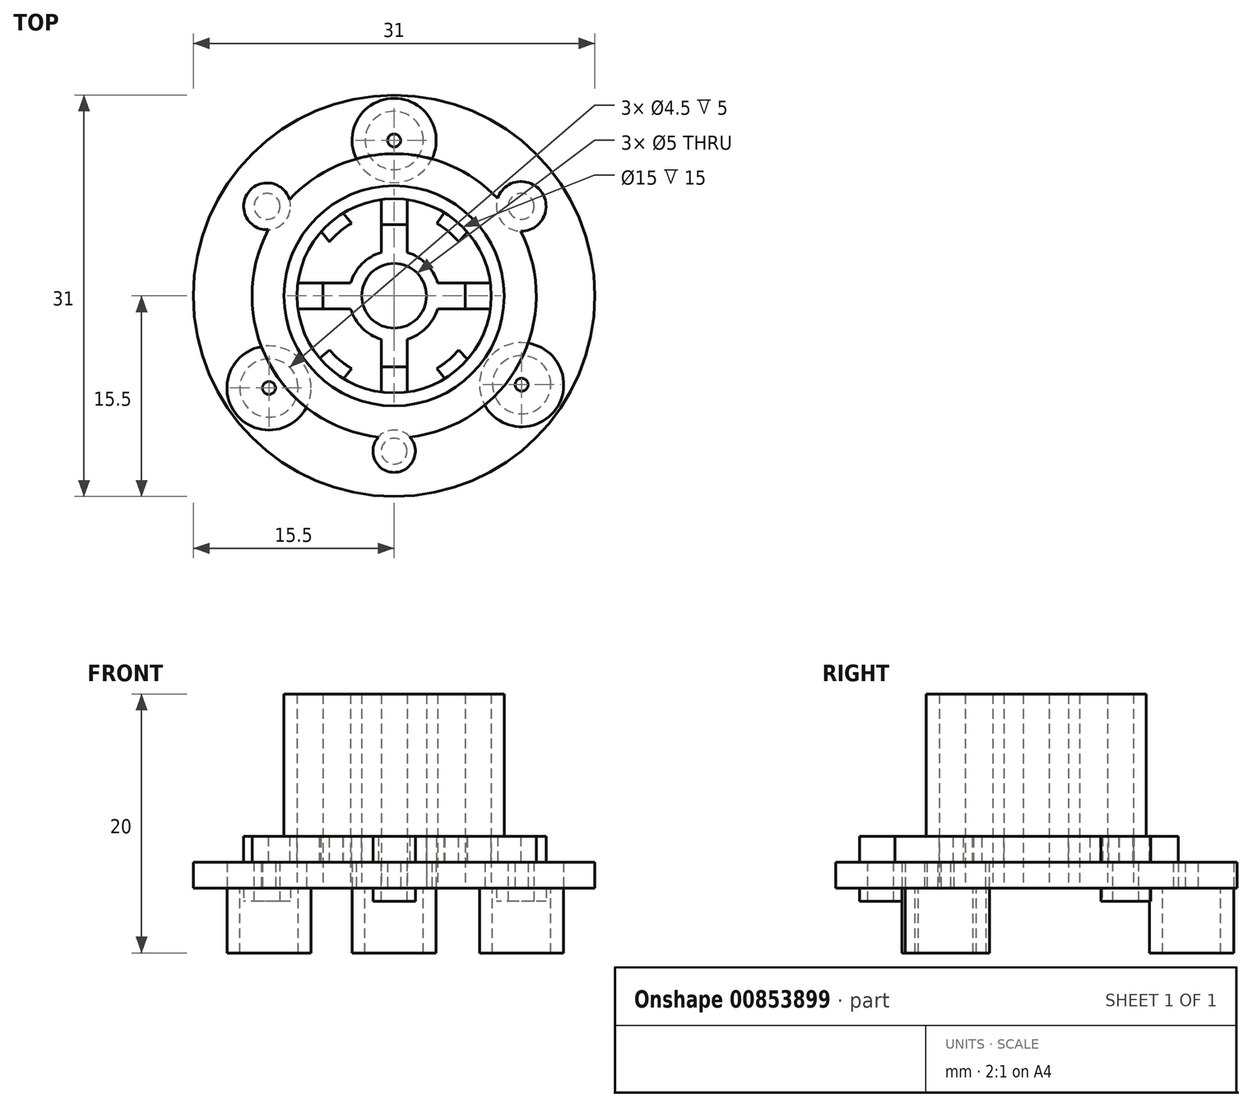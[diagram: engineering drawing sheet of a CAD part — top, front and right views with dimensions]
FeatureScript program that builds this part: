
annotation { "Feature Type Name" : "Feature", "Feature Type Description" : "" }
export const myFeature = defineFeature(function(context is Context, id is Id, definition is map)
    precondition{}
    {
        {
            var Q0;
            Q0=qCreatedBy(makeId("Top.planeOp"),FACE);
            var sketch = newSketch(context, id + "F0", { "sketchPlane" : qUnion([Q0])});
            skCircle(sketch, "E0", {"center": v(0, 0) * mm, "radius": 15.5 * mm});
            skCircle(sketch, "E1", {"center": v(0, 0) * mm, "radius": 8.5 * mm});
            skCircle(sketch, "E2.0", {"center": v(0, 0) * mm, "radius": 7.5 * mm});
            skLineSegment(sketch, "E3", {"start": v(-15.5, 0) * mm, "end": v(15.5, 0) * mm});
            skCircle(sketch, "E4", {"center": v(0, 0) * mm, "radius": 12 * mm});
            skCircle(sketch, "E5", {"center": v(0, 12) * mm, "radius": 3.25 * mm});
            skCircle(sketch, "E6", {"center": v(-9.66, -7.12) * mm, "radius": 3.25 * mm});
            skCircle(sketch, "E7", {"center": v(9.84, -6.87) * mm, "radius": 3.25 * mm});
            skCircle(sketch, "E8.0", {"center": v(-9.66, -7.12) * mm, "radius": 2.25 * mm});
            skCircle(sketch, "E9.0", {"center": v(9.84, -6.87) * mm, "radius": 2.25 * mm});
            skCircle(sketch, "E10.0", {"center": v(0, 12) * mm, "radius": 2.25 * mm});
            skCircle(sketch, "E11", {"center": v(0, -12) * mm, "radius": 1 * mm});
            skCircle(sketch, "E12", {"center": v(-9.81, 6.91) * mm, "radius": 1 * mm});
            skCircle(sketch, "E13", {"center": v(9.81, 6.91) * mm, "radius": 1 * mm});
            skCircle(sketch, "E14", {"center": v(0, 0) * mm, "radius": 10.97 * mm});
            skCircle(sketch, "E15", {"center": v(0, -12) * mm, "radius": 1.64 * mm});
            skCircle(sketch, "E16", {"center": v(9.81, 6.91) * mm, "radius": 1.92 * mm});
            skCircle(sketch, "E17", {"center": v(-9.81, 6.91) * mm, "radius": 1.8 * mm});
            skCircle(sketch, "E18", {"center": v(-9.66, -7.12) * mm, "radius": 0.5 * mm});
            skCircle(sketch, "E19", {"center": v(9.84, -6.87) * mm, "radius": 0.5 * mm});
            skCircle(sketch, "E20", {"center": v(0, 12) * mm, "radius": 0.5 * mm});
            skCircle(sketch, "E21", {"center": v(0, 0) * mm, "radius": 2.5 * mm});
            skLineSegment(sketch, "E22.bottom", {"start": v(1, -5.5) * mm, "end": v(-1, -5.5) * mm});
            skLineSegment(sketch, "E22.top", {"start": v(1, 5.5) * mm, "end": v(-1, 5.5) * mm});
            skLineSegment(sketch, "E22.left", {"start": v(1, -5.5) * mm, "end": v(1, 5.5) * mm});
            skLineSegment(sketch, "E22.right", {"start": v(-1, -5.5) * mm, "end": v(-1, 5.5) * mm});
            skLineSegment(sketch, "E23.bottom", {"start": v(5.5, -1) * mm, "end": v(-5.5, -1) * mm});
            skLineSegment(sketch, "E23.top", {"start": v(5.5, 1) * mm, "end": v(-5.5, 1) * mm});
            skLineSegment(sketch, "E23.left", {"start": v(5.5, -1) * mm, "end": v(5.5, 1) * mm});
            skLineSegment(sketch, "E23.right", {"start": v(-5.5, -1) * mm, "end": v(-5.5, 1) * mm});
            skCircle(sketch, "E24.0", {"center": v(0, 0) * mm, "radius": 3.5 * mm});
            skLineSegment(sketch, "E25", {"start": v(-5.5, -1) * mm, "end": v(-7.43, -1) * mm});
            skLineSegment(sketch, "E26", {"start": v(-5.5, 1) * mm, "end": v(-7.43, 1) * mm});
            skLineSegment(sketch, "E27", {"start": v(5.5, -1) * mm, "end": v(7.43, -1) * mm});
            skLineSegment(sketch, "E28", {"start": v(5.5, 1) * mm, "end": v(7.43, 1) * mm});
            skLineSegment(sketch, "E29", {"start": v(-1, -5.5) * mm, "end": v(-1, -7.43) * mm});
            skLineSegment(sketch, "E30", {"start": v(1, -5.5) * mm, "end": v(1, -7.43) * mm});
            skLineSegment(sketch, "E31", {"start": v(-1, 5.5) * mm, "end": v(-1, 7.43) * mm});
            skLineSegment(sketch, "E32", {"start": v(1, 5.5) * mm, "end": v(1, 7.43) * mm});
            skSolve(sketch);
        }
        {
            var Q0;
            Q0=makeQuery(id+"F0.imprint","IMPRINT",FACE,{"disambiguationData":[TD([[makeQuery(id+"F0.imprint","IMPRINT",EDGE,{"derivedFrom":sQuery(id+"F0.wireOp",EDGE,"E0")}),1.0]])]});
            var Q1;
            {var subQ0=sQuery(id+"F0.wireOp",EDGE,"S9bKF7eP-WOtO-HVjA-zyf9-2dM2ckVghxGc");var subQ4=sQuery(id+"F0.wireOp",EDGE,"a8cJaAZh-5I12-enwt-A6UE-ITXqOD4lF9Ac");var subQ5=makeQuery(id+"F0.imprint","INTERSECT",VERTEX,{"disambiguationData":[OD(0.0)],"derivedFrom":[subQ0,subQ4]});Q1=makeQuery(id+"F0.imprint","IMPRINT",FACE,{"disambiguationData":[TD([[makeQuery(id+"F0.imprint","IMPRINT",EDGE,{"disambiguationData":[TD([[subQ5,1.0]])],"derivedFrom":subQ4}),-1.0]])]});}
            var Q2;
            {var subQ1=sQuery(id+"F0.wireOp",EDGE,"E3");var subQ4=sQuery(id+"F0.wireOp",EDGE,"E1");var subQ11=makeQuery(id+"F0.imprint","INTERSECT",VERTEX,{"disambiguationData":[OD(0.0)],"derivedFrom":[subQ4,subQ1]});Q2=makeQuery(id+"F0.imprint","IMPRINT",FACE,{"disambiguationData":[TD([[makeQuery(id+"F0.imprint","IMPRINT",EDGE,{"disambiguationData":[TD([[subQ11,-1.0]])],"derivedFrom":subQ4}),-1.0]])]});}
            var Q3;
            {var subQ5=sQuery(id+"F0.wireOp",EDGE,"ll5ePz1X-QG4W-kVrY-982M-5qMvGsVVYmu8");Q3=makeQuery(id+"F0.imprint","IMPRINT",FACE,{"disambiguationData":[TD([[makeQuery(id+"F0.imprint","IMPRINT",EDGE,{"derivedFrom":subQ5}),-1.0]])]});}
            var Q4;
            {var subQ0=sQuery(id+"F0.wireOp",EDGE,"Ehf1EnBC-OwnA-8WcZ-1eJj-KpamyHMtwVbQ");var subQ4=sQuery(id+"F0.wireOp",EDGE,"xySDpFPR-NNtx-CsFH-j8Qs-mnjDACDE4txv");var subQ5=makeQuery(id+"F0.imprint","INTERSECT",VERTEX,{"disambiguationData":[OD(0.0)],"derivedFrom":[subQ0,subQ4]});Q4=makeQuery(id+"F0.imprint","IMPRINT",FACE,{"disambiguationData":[TD([[makeQuery(id+"F0.imprint","IMPRINT",EDGE,{"disambiguationData":[TD([[subQ5,1.0]])],"derivedFrom":subQ4}),-1.0]])]});}
            var Q5;
            {var subQ1=sQuery(id+"F0.wireOp",EDGE,"E3");var subQ5=sQuery(id+"F0.wireOp",EDGE,"E1");var subQ6=makeQuery(id+"F0.imprint","INTERSECT",VERTEX,{"disambiguationData":[OD(0.0)],"derivedFrom":[subQ5,subQ1]});Q5=makeQuery(id+"F0.imprint","IMPRINT",FACE,{"disambiguationData":[TD([[makeQuery(id+"F0.imprint","IMPRINT",EDGE,{"disambiguationData":[TD([[subQ6,1.0]])],"derivedFrom":subQ5}),-1.0]])]});}
            var Q6;
            {var subQ0=sQuery(id+"F0.wireOp",EDGE,"E3");var subQ1=sQuery(id+"F0.wireOp",EDGE,"E0");var subQ5=makeQuery(id+"F0.imprint","INTERSECT",VERTEX,{"disambiguationData":[OD(0.0)],"derivedFrom":[subQ1,subQ0]});Q6=makeQuery(id+"F0.imprint","IMPRINT",FACE,{"disambiguationData":[TD([[makeQuery(id+"F0.imprint","IMPRINT",EDGE,{"disambiguationData":[TD([[subQ5,-1.0]])],"derivedFrom":subQ1}),1.0]])]});}
            var Q7;
            {var subQ0=sQuery(id+"F0.wireOp",EDGE,"E6");var subQ1=sQuery(id+"F0.wireOp",EDGE,"E4");var subQ2=makeQuery(id+"F0.imprint","INTERSECT",VERTEX,{"disambiguationData":[OD(1.0)],"derivedFrom":[subQ1,subQ0]});Q7=makeQuery(id+"F0.imprint","IMPRINT",FACE,{"disambiguationData":[TD([[makeQuery(id+"F0.imprint","IMPRINT",EDGE,{"disambiguationData":[TD([[subQ2,-1.0]])],"derivedFrom":subQ1}),1.0]])]});}
            var Q8;
            {var subQ0=sQuery(id+"F0.wireOp",EDGE,"E4");var subQ1=sQuery(id+"F0.wireOp",EDGE,"E3");var subQ2=makeQuery(id+"F0.imprint","INTERSECT",VERTEX,{"disambiguationData":[OD(0.0)],"derivedFrom":[subQ1,subQ0]});Q8=makeQuery(id+"F0.imprint","IMPRINT",FACE,{"disambiguationData":[TD([[makeQuery(id+"F0.imprint","IMPRINT",EDGE,{"disambiguationData":[TD([[subQ2,-1.0]])],"derivedFrom":subQ1}),-1.0]])]});}
            var Q9;
            {var subQ0=sQuery(id+"F0.wireOp",EDGE,"E4");var subQ1=sQuery(id+"F0.wireOp",EDGE,"E3");var subQ2=makeQuery(id+"F0.imprint","INTERSECT",VERTEX,{"disambiguationData":[OD(0.0)],"derivedFrom":[subQ1,subQ0]});Q9=makeQuery(id+"F0.imprint","IMPRINT",FACE,{"disambiguationData":[TD([[makeQuery(id+"F0.imprint","IMPRINT",EDGE,{"disambiguationData":[TD([[subQ2,-1.0]])],"derivedFrom":subQ1}),1.0]])]});}
            var Q10;
            {var subQ0=sQuery(id+"F0.wireOp",EDGE,"E5");var subQ1=sQuery(id+"F0.wireOp",EDGE,"E4");var subQ2=makeQuery(id+"F0.imprint","INTERSECT",VERTEX,{"disambiguationData":[OD(1.0)],"derivedFrom":[subQ1,subQ0]});Q10=makeQuery(id+"F0.imprint","IMPRINT",FACE,{"disambiguationData":[TD([[makeQuery(id+"F0.imprint","IMPRINT",EDGE,{"disambiguationData":[TD([[subQ2,-1.0]])],"derivedFrom":subQ1}),1.0]])]});}
            var Q11;
            {var subQ0=sQuery(id+"F0.wireOp",EDGE,"E16");var subQ1=sQuery(id+"F0.wireOp",EDGE,"E4");var subQ2=makeQuery(id+"F0.imprint","INTERSECT",VERTEX,{"disambiguationData":[OD(1.0)],"derivedFrom":[subQ1,subQ0]});Q11=makeQuery(id+"F0.imprint","IMPRINT",FACE,{"disambiguationData":[TD([[makeQuery(id+"F0.imprint","IMPRINT",EDGE,{"disambiguationData":[TD([[subQ2,-1.0]])],"derivedFrom":subQ1}),1.0]])]});}
            var Q12;
            {var subQ0=sQuery(id+"F0.wireOp",EDGE,"E14");var subQ1=sQuery(id+"F0.wireOp",EDGE,"E3");var subQ2=makeQuery(id+"F0.imprint","INTERSECT",VERTEX,{"disambiguationData":[OD(1.0)],"derivedFrom":[subQ1,subQ0]});Q12=makeQuery(id+"F0.imprint","IMPRINT",FACE,{"disambiguationData":[TD([[makeQuery(id+"F0.imprint","IMPRINT",EDGE,{"disambiguationData":[TD([[subQ2,-1.0]])],"derivedFrom":subQ1}),1.0]])]});}
            var Q13;
            {var subQ0=sQuery(id+"F0.wireOp",EDGE,"E14");var subQ1=sQuery(id+"F0.wireOp",EDGE,"E3");var subQ2=makeQuery(id+"F0.imprint","INTERSECT",VERTEX,{"disambiguationData":[OD(1.0)],"derivedFrom":[subQ1,subQ0]});Q13=makeQuery(id+"F0.imprint","IMPRINT",FACE,{"disambiguationData":[TD([[makeQuery(id+"F0.imprint","IMPRINT",EDGE,{"disambiguationData":[TD([[subQ2,-1.0]])],"derivedFrom":subQ1}),-1.0]])]});}
            var Q14;
            {var subQ0=sQuery(id+"F0.wireOp",EDGE,"E15");var subQ1=sQuery(id+"F0.wireOp",EDGE,"E4");var subQ2=makeQuery(id+"F0.imprint","INTERSECT",VERTEX,{"disambiguationData":[OD(1.0)],"derivedFrom":[subQ1,subQ0]});Q14=makeQuery(id+"F0.imprint","IMPRINT",FACE,{"disambiguationData":[TD([[makeQuery(id+"F0.imprint","IMPRINT",EDGE,{"disambiguationData":[TD([[subQ2,-1.0]])],"derivedFrom":subQ1}),1.0]])]});}
            extrude(context, id + "F1", {"entities" : qUnion([Q0, Q1, Q2, Q3, Q4, Q5, Q6, Q7, Q8, Q9, Q10, Q11, Q12, Q13, Q14]), "depth" : 2 * mm, "offsetDistance" : 25 * mm});
        }
        {
            var Q0;
            Q0=makeQuery(id+"F0.imprint","IMPRINT",FACE,{"disambiguationData":[TD([[makeQuery(id+"F0.imprint","IMPRINT",EDGE,{"derivedFrom":sQuery(id+"F0.wireOp",EDGE,"E1")}),1.0]])]});
            extrude(context, id + "F2", {"entities" : qUnion([Q0]), "operationType" : NewBodyOperationType.ADD, "depth" : 15 * mm, "offsetDistance" : 25 * mm});
        }
        {
            var Q0;
            {var subQ0=sQuery(id+"F0.wireOp",EDGE,"E5");var subQ1=sQuery(id+"F0.wireOp",EDGE,"E4");var subQ2=makeQuery(id+"F0.imprint","INTERSECT",VERTEX,{"disambiguationData":[OD(0.0)],"derivedFrom":[subQ1,subQ0]});Q0=makeQuery(id+"F0.imprint","IMPRINT",FACE,{"disambiguationData":[TD([[makeQuery(id+"F0.imprint","IMPRINT",EDGE,{"disambiguationData":[TD([[subQ2,-1.0]])],"derivedFrom":subQ1}),-1.0]])]});}
            var Q1;
            {var subQ0=sQuery(id+"F0.wireOp",EDGE,"E5");var subQ1=sQuery(id+"F0.wireOp",EDGE,"E4");var subQ2=makeQuery(id+"F0.imprint","INTERSECT",VERTEX,{"disambiguationData":[OD(0.0)],"derivedFrom":[subQ1,subQ0]});Q1=makeQuery(id+"F0.imprint","IMPRINT",FACE,{"disambiguationData":[TD([[makeQuery(id+"F0.imprint","IMPRINT",EDGE,{"disambiguationData":[TD([[subQ2,-1.0]])],"derivedFrom":subQ1}),1.0]])]});}
            var Q2;
            {var subQ0=sQuery(id+"F0.wireOp",EDGE,"E7");var subQ1=sQuery(id+"F0.wireOp",EDGE,"E4");var subQ2=makeQuery(id+"F0.imprint","INTERSECT",VERTEX,{"disambiguationData":[OD(0.0)],"derivedFrom":[subQ1,subQ0]});Q2=makeQuery(id+"F0.imprint","IMPRINT",FACE,{"disambiguationData":[TD([[makeQuery(id+"F0.imprint","IMPRINT",EDGE,{"disambiguationData":[TD([[subQ2,-1.0]])],"derivedFrom":subQ1}),1.0]])]});}
            var Q3;
            {var subQ0=sQuery(id+"F0.wireOp",EDGE,"E7");var subQ1=sQuery(id+"F0.wireOp",EDGE,"E4");var subQ2=makeQuery(id+"F0.imprint","INTERSECT",VERTEX,{"disambiguationData":[OD(0.0)],"derivedFrom":[subQ1,subQ0]});Q3=makeQuery(id+"F0.imprint","IMPRINT",FACE,{"disambiguationData":[TD([[makeQuery(id+"F0.imprint","IMPRINT",EDGE,{"disambiguationData":[TD([[subQ2,-1.0]])],"derivedFrom":subQ1}),-1.0]])]});}
            var Q4;
            {var subQ0=sQuery(id+"F0.wireOp",EDGE,"E6");var subQ1=sQuery(id+"F0.wireOp",EDGE,"E4");var subQ2=makeQuery(id+"F0.imprint","INTERSECT",VERTEX,{"disambiguationData":[OD(0.0)],"derivedFrom":[subQ1,subQ0]});Q4=makeQuery(id+"F0.imprint","IMPRINT",FACE,{"disambiguationData":[TD([[makeQuery(id+"F0.imprint","IMPRINT",EDGE,{"disambiguationData":[TD([[subQ2,-1.0]])],"derivedFrom":subQ1}),-1.0]])]});}
            var Q5;
            {var subQ0=sQuery(id+"F0.wireOp",EDGE,"E6");var subQ1=sQuery(id+"F0.wireOp",EDGE,"E4");var subQ2=makeQuery(id+"F0.imprint","INTERSECT",VERTEX,{"disambiguationData":[OD(0.0)],"derivedFrom":[subQ1,subQ0]});Q5=makeQuery(id+"F0.imprint","IMPRINT",FACE,{"disambiguationData":[TD([[makeQuery(id+"F0.imprint","IMPRINT",EDGE,{"disambiguationData":[TD([[subQ2,-1.0]])],"derivedFrom":subQ1}),1.0]])]});}
            var Q6;
            {var subQ0=sQuery(id+"F0.wireOp",EDGE,"E14");var subQ1=sQuery(id+"F0.wireOp",EDGE,"E6");var subQ2=makeQuery(id+"F0.imprint","INTERSECT",VERTEX,{"disambiguationData":[OD(0.0)],"derivedFrom":[subQ1,subQ0]});Q6=makeQuery(id+"F0.imprint","IMPRINT",FACE,{"disambiguationData":[TD([[makeQuery(id+"F0.imprint","IMPRINT",EDGE,{"disambiguationData":[TD([[subQ2,1.0]])],"derivedFrom":subQ1}),1.0]])]});}
            var Q7;
            {var subQ0=sQuery(id+"F0.wireOp",EDGE,"E8.0");var subQ1=sQuery(id+"F0.wireOp",EDGE,"E4");var subQ2=makeQuery(id+"F0.imprint","INTERSECT",VERTEX,{"disambiguationData":[OD(1.0)],"derivedFrom":[subQ1,subQ0]});Q7=makeQuery(id+"F0.imprint","IMPRINT",FACE,{"disambiguationData":[TD([[makeQuery(id+"F0.imprint","IMPRINT",EDGE,{"disambiguationData":[TD([[subQ2,-1.0]])],"derivedFrom":subQ1}),1.0]])]});}
            var Q8;
            {var subQ0=sQuery(id+"F0.wireOp",EDGE,"E14");var subQ1=sQuery(id+"F0.wireOp",EDGE,"E7");var subQ2=makeQuery(id+"F0.imprint","INTERSECT",VERTEX,{"disambiguationData":[OD(0.0)],"derivedFrom":[subQ1,subQ0]});Q8=makeQuery(id+"F0.imprint","IMPRINT",FACE,{"disambiguationData":[TD([[makeQuery(id+"F0.imprint","IMPRINT",EDGE,{"disambiguationData":[TD([[subQ2,-1.0]])],"derivedFrom":subQ1}),1.0]])]});}
            var Q9;
            {var subQ0=sQuery(id+"F0.wireOp",EDGE,"E9.0");var subQ1=sQuery(id+"F0.wireOp",EDGE,"E4");var subQ2=makeQuery(id+"F0.imprint","INTERSECT",VERTEX,{"disambiguationData":[OD(1.0)],"derivedFrom":[subQ1,subQ0]});Q9=makeQuery(id+"F0.imprint","IMPRINT",FACE,{"disambiguationData":[TD([[makeQuery(id+"F0.imprint","IMPRINT",EDGE,{"disambiguationData":[TD([[subQ2,-1.0]])],"derivedFrom":subQ1}),1.0]])]});}
            var Q10;
            {var subQ0=sQuery(id+"F0.wireOp",EDGE,"E14");var subQ1=sQuery(id+"F0.wireOp",EDGE,"E5");var subQ2=makeQuery(id+"F0.imprint","INTERSECT",VERTEX,{"disambiguationData":[OD(0.0)],"derivedFrom":[subQ1,subQ0]});Q10=makeQuery(id+"F0.imprint","IMPRINT",FACE,{"disambiguationData":[TD([[makeQuery(id+"F0.imprint","IMPRINT",EDGE,{"disambiguationData":[TD([[subQ2,-1.0]])],"derivedFrom":subQ1}),1.0]])]});}
            var Q11;
            {var subQ0=sQuery(id+"F0.wireOp",EDGE,"E10.0");var subQ1=sQuery(id+"F0.wireOp",EDGE,"E4");var subQ2=makeQuery(id+"F0.imprint","INTERSECT",VERTEX,{"disambiguationData":[OD(1.0)],"derivedFrom":[subQ1,subQ0]});Q11=makeQuery(id+"F0.imprint","IMPRINT",FACE,{"disambiguationData":[TD([[makeQuery(id+"F0.imprint","IMPRINT",EDGE,{"disambiguationData":[TD([[subQ2,-1.0]])],"derivedFrom":subQ1}),1.0]])]});}
            extrude(context, id + "F3", {"entities" : qUnion([Q0, Q1, Q2, Q3, Q4, Q5, Q6, Q7, Q8, Q9, Q10, Q11]), "depth" : -5 * mm, "offsetDistance" : 25 * mm});
        }
        {
            var Q0;
            {var subQ0=sQuery(id+"F0.wireOp",EDGE,"E3");var subQ1=sQuery(id+"F0.wireOp",EDGE,"E1");var subQ2=makeQuery(id+"F0.imprint","INTERSECT",VERTEX,{"disambiguationData":[OD(0.0)],"derivedFrom":[subQ1,subQ0]});Q0=makeQuery(id+"F0.imprint","IMPRINT",FACE,{"disambiguationData":[TD([[makeQuery(id+"F0.imprint","IMPRINT",EDGE,{"disambiguationData":[TD([[subQ2,1.0]])],"derivedFrom":subQ1}),-1.0]])]});}
            var Q1;
            {var subQ0=sQuery(id+"F0.wireOp",EDGE,"E3");var subQ1=sQuery(id+"F0.wireOp",EDGE,"E1");var subQ11=makeQuery(id+"F0.imprint","INTERSECT",VERTEX,{"disambiguationData":[OD(0.0)],"derivedFrom":[subQ1,subQ0]});Q1=makeQuery(id+"F0.imprint","IMPRINT",FACE,{"disambiguationData":[TD([[makeQuery(id+"F0.imprint","IMPRINT",EDGE,{"disambiguationData":[TD([[subQ11,-1.0]])],"derivedFrom":subQ1}),-1.0]])]});}
            var Q2;
            {var subQ0=sQuery(id+"F0.wireOp",EDGE,"E14");var subQ1=sQuery(id+"F0.wireOp",EDGE,"E6");var subQ2=makeQuery(id+"F0.imprint","INTERSECT",VERTEX,{"disambiguationData":[OD(0.0)],"derivedFrom":[subQ1,subQ0]});Q2=makeQuery(id+"F0.imprint","IMPRINT",FACE,{"disambiguationData":[TD([[makeQuery(id+"F0.imprint","IMPRINT",EDGE,{"disambiguationData":[TD([[subQ2,1.0]])],"derivedFrom":subQ1}),1.0]])]});}
            var Q3;
            {var subQ0=sQuery(id+"F0.wireOp",EDGE,"E14");var subQ1=sQuery(id+"F0.wireOp",EDGE,"E8.0");var subQ2=makeQuery(id+"F0.imprint","INTERSECT",VERTEX,{"disambiguationData":[OD(0.0)],"derivedFrom":[subQ1,subQ0]});Q3=makeQuery(id+"F0.imprint","IMPRINT",FACE,{"disambiguationData":[TD([[makeQuery(id+"F0.imprint","IMPRINT",EDGE,{"disambiguationData":[TD([[subQ2,1.0]])],"derivedFrom":subQ1}),1.0]])]});}
            var Q4;
            {var subQ0=sQuery(id+"F0.wireOp",EDGE,"E17");var subQ1=sQuery(id+"F0.wireOp",EDGE,"E14");var subQ2=makeQuery(id+"F0.imprint","INTERSECT",VERTEX,{"disambiguationData":[OD(0.0)],"derivedFrom":[subQ1,subQ0]});Q4=makeQuery(id+"F0.imprint","IMPRINT",FACE,{"disambiguationData":[TD([[makeQuery(id+"F0.imprint","IMPRINT",EDGE,{"disambiguationData":[TD([[subQ2,-1.0]])],"derivedFrom":subQ1}),1.0]])]});}
            var Q5;
            {var subQ0=sQuery(id+"F0.wireOp",EDGE,"E17");var subQ1=sQuery(id+"F0.wireOp",EDGE,"E4");var subQ2=makeQuery(id+"F0.imprint","INTERSECT",VERTEX,{"disambiguationData":[OD(0.0)],"derivedFrom":[subQ1,subQ0]});Q5=makeQuery(id+"F0.imprint","IMPRINT",FACE,{"disambiguationData":[TD([[makeQuery(id+"F0.imprint","IMPRINT",EDGE,{"disambiguationData":[TD([[subQ2,-1.0]])],"derivedFrom":subQ1}),-1.0]])]});}
            var Q6;
            {var subQ0=sQuery(id+"F0.wireOp",EDGE,"E17");var subQ5=sQuery(id+"F0.wireOp",EDGE,"E4");var subQ8=makeQuery(id+"F0.imprint","INTERSECT",VERTEX,{"disambiguationData":[OD(0.0)],"derivedFrom":[subQ5,subQ0]});Q6=makeQuery(id+"F0.imprint","IMPRINT",FACE,{"disambiguationData":[TD([[makeQuery(id+"F0.imprint","IMPRINT",EDGE,{"disambiguationData":[TD([[subQ8,-1.0]])],"derivedFrom":subQ5}),1.0]])]});}
            var Q7;
            {var subQ0=sQuery(id+"F0.wireOp",EDGE,"E12");var subQ1=sQuery(id+"F0.wireOp",EDGE,"E4");var subQ2=makeQuery(id+"F0.imprint","INTERSECT",VERTEX,{"disambiguationData":[OD(0.0)],"derivedFrom":[subQ1,subQ0]});Q7=makeQuery(id+"F0.imprint","IMPRINT",FACE,{"disambiguationData":[TD([[makeQuery(id+"F0.imprint","IMPRINT",EDGE,{"disambiguationData":[TD([[subQ2,-1.0]])],"derivedFrom":subQ1}),1.0]])]});}
            var Q8;
            {var subQ0=sQuery(id+"F0.wireOp",EDGE,"E12");var subQ1=sQuery(id+"F0.wireOp",EDGE,"E4");var subQ2=makeQuery(id+"F0.imprint","INTERSECT",VERTEX,{"disambiguationData":[OD(0.0)],"derivedFrom":[subQ1,subQ0]});Q8=makeQuery(id+"F0.imprint","IMPRINT",FACE,{"disambiguationData":[TD([[makeQuery(id+"F0.imprint","IMPRINT",EDGE,{"disambiguationData":[TD([[subQ2,-1.0]])],"derivedFrom":subQ1}),-1.0]])]});}
            var Q9;
            {var subQ0=sQuery(id+"F0.wireOp",EDGE,"E16");var subQ1=sQuery(id+"F0.wireOp",EDGE,"E4");var subQ2=makeQuery(id+"F0.imprint","INTERSECT",VERTEX,{"disambiguationData":[OD(0.0)],"derivedFrom":[subQ1,subQ0]});Q9=makeQuery(id+"F0.imprint","IMPRINT",FACE,{"disambiguationData":[TD([[makeQuery(id+"F0.imprint","IMPRINT",EDGE,{"disambiguationData":[TD([[subQ2,-1.0]])],"derivedFrom":subQ1}),-1.0]])]});}
            var Q10;
            {var subQ0=sQuery(id+"F0.wireOp",EDGE,"E13");var subQ1=sQuery(id+"F0.wireOp",EDGE,"E4");var subQ2=makeQuery(id+"F0.imprint","INTERSECT",VERTEX,{"disambiguationData":[OD(0.0)],"derivedFrom":[subQ1,subQ0]});Q10=makeQuery(id+"F0.imprint","IMPRINT",FACE,{"disambiguationData":[TD([[makeQuery(id+"F0.imprint","IMPRINT",EDGE,{"disambiguationData":[TD([[subQ2,-1.0]])],"derivedFrom":subQ1}),-1.0]])]});}
            var Q11;
            {var subQ0=sQuery(id+"F0.wireOp",EDGE,"E13");var subQ1=sQuery(id+"F0.wireOp",EDGE,"E4");var subQ2=makeQuery(id+"F0.imprint","INTERSECT",VERTEX,{"disambiguationData":[OD(0.0)],"derivedFrom":[subQ1,subQ0]});Q11=makeQuery(id+"F0.imprint","IMPRINT",FACE,{"disambiguationData":[TD([[makeQuery(id+"F0.imprint","IMPRINT",EDGE,{"disambiguationData":[TD([[subQ2,-1.0]])],"derivedFrom":subQ1}),1.0]])]});}
            var Q12;
            {var subQ0=sQuery(id+"F0.wireOp",EDGE,"E16");var subQ5=sQuery(id+"F0.wireOp",EDGE,"E4");var subQ9=makeQuery(id+"F0.imprint","INTERSECT",VERTEX,{"disambiguationData":[OD(0.0)],"derivedFrom":[subQ5,subQ0]});Q12=makeQuery(id+"F0.imprint","IMPRINT",FACE,{"disambiguationData":[TD([[makeQuery(id+"F0.imprint","IMPRINT",EDGE,{"disambiguationData":[TD([[subQ9,-1.0]])],"derivedFrom":subQ5}),1.0]])]});}
            var Q13;
            {var subQ0=sQuery(id+"F0.wireOp",EDGE,"E16");var subQ1=sQuery(id+"F0.wireOp",EDGE,"E14");var subQ2=makeQuery(id+"F0.imprint","INTERSECT",VERTEX,{"disambiguationData":[OD(0.0)],"derivedFrom":[subQ1,subQ0]});Q13=makeQuery(id+"F0.imprint","IMPRINT",FACE,{"disambiguationData":[TD([[makeQuery(id+"F0.imprint","IMPRINT",EDGE,{"disambiguationData":[TD([[subQ2,-1.0]])],"derivedFrom":subQ1}),1.0]])]});}
            var Q14;
            {var subQ0=sQuery(id+"F0.wireOp",EDGE,"E14");var subQ1=sQuery(id+"F0.wireOp",EDGE,"E9.0");var subQ2=makeQuery(id+"F0.imprint","INTERSECT",VERTEX,{"disambiguationData":[OD(0.0)],"derivedFrom":[subQ1,subQ0]});Q14=makeQuery(id+"F0.imprint","IMPRINT",FACE,{"disambiguationData":[TD([[makeQuery(id+"F0.imprint","IMPRINT",EDGE,{"disambiguationData":[TD([[subQ2,-1.0]])],"derivedFrom":subQ1}),1.0]])]});}
            var Q15;
            {var subQ0=sQuery(id+"F0.wireOp",EDGE,"E14");var subQ1=sQuery(id+"F0.wireOp",EDGE,"E7");var subQ2=makeQuery(id+"F0.imprint","INTERSECT",VERTEX,{"disambiguationData":[OD(0.0)],"derivedFrom":[subQ1,subQ0]});Q15=makeQuery(id+"F0.imprint","IMPRINT",FACE,{"disambiguationData":[TD([[makeQuery(id+"F0.imprint","IMPRINT",EDGE,{"disambiguationData":[TD([[subQ2,-1.0]])],"derivedFrom":subQ1}),1.0]])]});}
            var Q16;
            {var subQ0=sQuery(id+"F0.wireOp",EDGE,"E11");var subQ1=sQuery(id+"F0.wireOp",EDGE,"E4");var subQ2=makeQuery(id+"F0.imprint","INTERSECT",VERTEX,{"disambiguationData":[OD(0.0)],"derivedFrom":[subQ1,subQ0]});Q16=makeQuery(id+"F0.imprint","IMPRINT",FACE,{"disambiguationData":[TD([[makeQuery(id+"F0.imprint","IMPRINT",EDGE,{"disambiguationData":[TD([[subQ2,-1.0]])],"derivedFrom":subQ1}),1.0]])]});}
            var Q17;
            {var subQ0=sQuery(id+"F0.wireOp",EDGE,"E11");var subQ1=sQuery(id+"F0.wireOp",EDGE,"E4");var subQ2=makeQuery(id+"F0.imprint","INTERSECT",VERTEX,{"disambiguationData":[OD(0.0)],"derivedFrom":[subQ1,subQ0]});Q17=makeQuery(id+"F0.imprint","IMPRINT",FACE,{"disambiguationData":[TD([[makeQuery(id+"F0.imprint","IMPRINT",EDGE,{"disambiguationData":[TD([[subQ2,-1.0]])],"derivedFrom":subQ1}),-1.0]])]});}
            var Q18;
            {var subQ0=sQuery(id+"F0.wireOp",EDGE,"E15");var subQ1=sQuery(id+"F0.wireOp",EDGE,"E14");var subQ2=makeQuery(id+"F0.imprint","INTERSECT",VERTEX,{"disambiguationData":[OD(0.0)],"derivedFrom":[subQ1,subQ0]});Q18=makeQuery(id+"F0.imprint","IMPRINT",FACE,{"disambiguationData":[TD([[makeQuery(id+"F0.imprint","IMPRINT",EDGE,{"disambiguationData":[TD([[subQ2,-1.0]])],"derivedFrom":subQ1}),1.0]])]});}
            var Q19;
            {var subQ0=sQuery(id+"F0.wireOp",EDGE,"E15");var subQ1=sQuery(id+"F0.wireOp",EDGE,"E4");var subQ2=makeQuery(id+"F0.imprint","INTERSECT",VERTEX,{"disambiguationData":[OD(0.0)],"derivedFrom":[subQ1,subQ0]});Q19=makeQuery(id+"F0.imprint","IMPRINT",FACE,{"disambiguationData":[TD([[makeQuery(id+"F0.imprint","IMPRINT",EDGE,{"disambiguationData":[TD([[subQ2,-1.0]])],"derivedFrom":subQ1}),-1.0]])]});}
            var Q20;
            {var subQ0=sQuery(id+"F0.wireOp",EDGE,"E15");var subQ5=sQuery(id+"F0.wireOp",EDGE,"E4");var subQ9=makeQuery(id+"F0.imprint","INTERSECT",VERTEX,{"disambiguationData":[OD(0.0)],"derivedFrom":[subQ5,subQ0]});Q20=makeQuery(id+"F0.imprint","IMPRINT",FACE,{"disambiguationData":[TD([[makeQuery(id+"F0.imprint","IMPRINT",EDGE,{"disambiguationData":[TD([[subQ9,-1.0]])],"derivedFrom":subQ5}),1.0]])]});}
            var Q21;
            {var subQ0=sQuery(id+"F0.wireOp",EDGE,"E14");var subQ1=sQuery(id+"F0.wireOp",EDGE,"E10.0");var subQ2=makeQuery(id+"F0.imprint","INTERSECT",VERTEX,{"disambiguationData":[OD(0.0)],"derivedFrom":[subQ1,subQ0]});Q21=makeQuery(id+"F0.imprint","IMPRINT",FACE,{"disambiguationData":[TD([[makeQuery(id+"F0.imprint","IMPRINT",EDGE,{"disambiguationData":[TD([[subQ2,-1.0]])],"derivedFrom":subQ1}),1.0]])]});}
            var Q22;
            {var subQ0=sQuery(id+"F0.wireOp",EDGE,"E14");var subQ1=sQuery(id+"F0.wireOp",EDGE,"E5");var subQ2=makeQuery(id+"F0.imprint","INTERSECT",VERTEX,{"disambiguationData":[OD(0.0)],"derivedFrom":[subQ1,subQ0]});Q22=makeQuery(id+"F0.imprint","IMPRINT",FACE,{"disambiguationData":[TD([[makeQuery(id+"F0.imprint","IMPRINT",EDGE,{"disambiguationData":[TD([[subQ2,-1.0]])],"derivedFrom":subQ1}),1.0]])]});}
            extrude(context, id + "F4", {"entities" : qUnion([Q0, Q1, Q2, Q3, Q4, Q5, Q6, Q7, Q8, Q9, Q10, Q11, Q12, Q13, Q14, Q15, Q16, Q17, Q18, Q19, Q20, Q21, Q22]), "depth" : 4 * mm, "offsetDistance" : 25 * mm});
        }
        {
            var Q0;
            {var subQ0=sQuery(id+"F0.wireOp",EDGE,"E9.0");var subQ1=sQuery(id+"F0.wireOp",EDGE,"E4");var subQ2=makeQuery(id+"F0.imprint","INTERSECT",VERTEX,{"disambiguationData":[OD(0.0)],"derivedFrom":[subQ1,subQ0]});Q0=makeQuery(id+"F0.imprint","IMPRINT",FACE,{"disambiguationData":[TD([[makeQuery(id+"F0.imprint","IMPRINT",EDGE,{"disambiguationData":[TD([[subQ2,-1.0]])],"derivedFrom":subQ1}),-1.0]])]});}
            var Q1;
            {var subQ0=sQuery(id+"F0.wireOp",EDGE,"E7");var subQ1=sQuery(id+"F0.wireOp",EDGE,"E4");var subQ2=makeQuery(id+"F0.imprint","INTERSECT",VERTEX,{"disambiguationData":[OD(0.0)],"derivedFrom":[subQ1,subQ0]});Q1=makeQuery(id+"F0.imprint","IMPRINT",FACE,{"disambiguationData":[TD([[makeQuery(id+"F0.imprint","IMPRINT",EDGE,{"disambiguationData":[TD([[subQ2,-1.0]])],"derivedFrom":subQ1}),-1.0]])]});}
            var Q2;
            {var subQ0=sQuery(id+"F0.wireOp",EDGE,"E9.0");var subQ1=sQuery(id+"F0.wireOp",EDGE,"E4");var subQ2=makeQuery(id+"F0.imprint","INTERSECT",VERTEX,{"disambiguationData":[OD(0.0)],"derivedFrom":[subQ1,subQ0]});Q2=makeQuery(id+"F0.imprint","IMPRINT",FACE,{"disambiguationData":[TD([[makeQuery(id+"F0.imprint","IMPRINT",EDGE,{"disambiguationData":[TD([[subQ2,-1.0]])],"derivedFrom":subQ1}),1.0]])]});}
            var Q3;
            {var subQ0=sQuery(id+"F0.wireOp",EDGE,"E7");var subQ1=sQuery(id+"F0.wireOp",EDGE,"E4");var subQ2=makeQuery(id+"F0.imprint","INTERSECT",VERTEX,{"disambiguationData":[OD(0.0)],"derivedFrom":[subQ1,subQ0]});Q3=makeQuery(id+"F0.imprint","IMPRINT",FACE,{"disambiguationData":[TD([[makeQuery(id+"F0.imprint","IMPRINT",EDGE,{"disambiguationData":[TD([[subQ2,-1.0]])],"derivedFrom":subQ1}),1.0]])]});}
            var Q4;
            {var subQ0=sQuery(id+"F0.wireOp",EDGE,"E9.0");var subQ1=sQuery(id+"F0.wireOp",EDGE,"E4");var subQ2=makeQuery(id+"F0.imprint","INTERSECT",VERTEX,{"disambiguationData":[OD(1.0)],"derivedFrom":[subQ1,subQ0]});Q4=makeQuery(id+"F0.imprint","IMPRINT",FACE,{"disambiguationData":[TD([[makeQuery(id+"F0.imprint","IMPRINT",EDGE,{"disambiguationData":[TD([[subQ2,-1.0]])],"derivedFrom":subQ1}),1.0]])]});}
            var Q5;
            {var subQ0=sQuery(id+"F0.wireOp",EDGE,"E8.0");var subQ1=sQuery(id+"F0.wireOp",EDGE,"E4");var subQ2=makeQuery(id+"F0.imprint","INTERSECT",VERTEX,{"disambiguationData":[OD(1.0)],"derivedFrom":[subQ1,subQ0]});Q5=makeQuery(id+"F0.imprint","IMPRINT",FACE,{"disambiguationData":[TD([[makeQuery(id+"F0.imprint","IMPRINT",EDGE,{"disambiguationData":[TD([[subQ2,-1.0]])],"derivedFrom":subQ1}),1.0]])]});}
            var Q6;
            {var subQ0=sQuery(id+"F0.wireOp",EDGE,"E8.0");var subQ1=sQuery(id+"F0.wireOp",EDGE,"E4");var subQ2=makeQuery(id+"F0.imprint","INTERSECT",VERTEX,{"disambiguationData":[OD(0.0)],"derivedFrom":[subQ1,subQ0]});Q6=makeQuery(id+"F0.imprint","IMPRINT",FACE,{"disambiguationData":[TD([[makeQuery(id+"F0.imprint","IMPRINT",EDGE,{"disambiguationData":[TD([[subQ2,-1.0]])],"derivedFrom":subQ1}),1.0]])]});}
            var Q7;
            {var subQ0=sQuery(id+"F0.wireOp",EDGE,"E6");var subQ1=sQuery(id+"F0.wireOp",EDGE,"E4");var subQ2=makeQuery(id+"F0.imprint","INTERSECT",VERTEX,{"disambiguationData":[OD(0.0)],"derivedFrom":[subQ1,subQ0]});Q7=makeQuery(id+"F0.imprint","IMPRINT",FACE,{"disambiguationData":[TD([[makeQuery(id+"F0.imprint","IMPRINT",EDGE,{"disambiguationData":[TD([[subQ2,-1.0]])],"derivedFrom":subQ1}),1.0]])]});}
            var Q8;
            {var subQ0=sQuery(id+"F0.wireOp",EDGE,"E6");var subQ1=sQuery(id+"F0.wireOp",EDGE,"E4");var subQ2=makeQuery(id+"F0.imprint","INTERSECT",VERTEX,{"disambiguationData":[OD(0.0)],"derivedFrom":[subQ1,subQ0]});Q8=makeQuery(id+"F0.imprint","IMPRINT",FACE,{"disambiguationData":[TD([[makeQuery(id+"F0.imprint","IMPRINT",EDGE,{"disambiguationData":[TD([[subQ2,-1.0]])],"derivedFrom":subQ1}),-1.0]])]});}
            var Q9;
            {var subQ0=sQuery(id+"F0.wireOp",EDGE,"E8.0");var subQ1=sQuery(id+"F0.wireOp",EDGE,"E4");var subQ2=makeQuery(id+"F0.imprint","INTERSECT",VERTEX,{"disambiguationData":[OD(0.0)],"derivedFrom":[subQ1,subQ0]});Q9=makeQuery(id+"F0.imprint","IMPRINT",FACE,{"disambiguationData":[TD([[makeQuery(id+"F0.imprint","IMPRINT",EDGE,{"disambiguationData":[TD([[subQ2,-1.0]])],"derivedFrom":subQ1}),-1.0]])]});}
            var Q10;
            {var subQ0=sQuery(id+"F0.wireOp",EDGE,"E10.0");var subQ1=sQuery(id+"F0.wireOp",EDGE,"E4");var subQ2=makeQuery(id+"F0.imprint","INTERSECT",VERTEX,{"disambiguationData":[OD(0.0)],"derivedFrom":[subQ1,subQ0]});Q10=makeQuery(id+"F0.imprint","IMPRINT",FACE,{"disambiguationData":[TD([[makeQuery(id+"F0.imprint","IMPRINT",EDGE,{"disambiguationData":[TD([[subQ2,-1.0]])],"derivedFrom":subQ1}),-1.0]])]});}
            var Q11;
            {var subQ0=sQuery(id+"F0.wireOp",EDGE,"E10.0");var subQ1=sQuery(id+"F0.wireOp",EDGE,"E4");var subQ2=makeQuery(id+"F0.imprint","INTERSECT",VERTEX,{"disambiguationData":[OD(1.0)],"derivedFrom":[subQ1,subQ0]});Q11=makeQuery(id+"F0.imprint","IMPRINT",FACE,{"disambiguationData":[TD([[makeQuery(id+"F0.imprint","IMPRINT",EDGE,{"disambiguationData":[TD([[subQ2,-1.0]])],"derivedFrom":subQ1}),1.0]])]});}
            var Q12;
            {var subQ0=sQuery(id+"F0.wireOp",EDGE,"E10.0");var subQ1=sQuery(id+"F0.wireOp",EDGE,"E4");var subQ2=makeQuery(id+"F0.imprint","INTERSECT",VERTEX,{"disambiguationData":[OD(0.0)],"derivedFrom":[subQ1,subQ0]});Q12=makeQuery(id+"F0.imprint","IMPRINT",FACE,{"disambiguationData":[TD([[makeQuery(id+"F0.imprint","IMPRINT",EDGE,{"disambiguationData":[TD([[subQ2,-1.0]])],"derivedFrom":subQ1}),1.0]])]});}
            var Q13;
            {var subQ0=sQuery(id+"F0.wireOp",EDGE,"E5");var subQ1=sQuery(id+"F0.wireOp",EDGE,"E4");var subQ2=makeQuery(id+"F0.imprint","INTERSECT",VERTEX,{"disambiguationData":[OD(0.0)],"derivedFrom":[subQ1,subQ0]});Q13=makeQuery(id+"F0.imprint","IMPRINT",FACE,{"disambiguationData":[TD([[makeQuery(id+"F0.imprint","IMPRINT",EDGE,{"disambiguationData":[TD([[subQ2,-1.0]])],"derivedFrom":subQ1}),1.0]])]});}
            var Q14;
            {var subQ0=sQuery(id+"F0.wireOp",EDGE,"E5");var subQ1=sQuery(id+"F0.wireOp",EDGE,"E4");var subQ2=makeQuery(id+"F0.imprint","INTERSECT",VERTEX,{"disambiguationData":[OD(0.0)],"derivedFrom":[subQ1,subQ0]});Q14=makeQuery(id+"F0.imprint","IMPRINT",FACE,{"disambiguationData":[TD([[makeQuery(id+"F0.imprint","IMPRINT",EDGE,{"disambiguationData":[TD([[subQ2,-1.0]])],"derivedFrom":subQ1}),-1.0]])]});}
            extrude(context, id + "F5", {"entities" : qUnion([Q0, Q1, Q2, Q3, Q4, Q5, Q6, Q7, Q8, Q9, Q10, Q11, Q12, Q13, Q14]), "depth" : 2 * mm, "offsetDistance" : 25 * mm});
        }
        {
            var Q0;
            {var subQ0=sQuery(id+"F0.wireOp",EDGE,"E17");var subQ1=sQuery(id+"F0.wireOp",EDGE,"E14");var subQ2=makeQuery(id+"F0.imprint","INTERSECT",VERTEX,{"disambiguationData":[OD(0.0)],"derivedFrom":[subQ1,subQ0]});Q0=makeQuery(id+"F0.imprint","IMPRINT",FACE,{"disambiguationData":[TD([[makeQuery(id+"F0.imprint","IMPRINT",EDGE,{"disambiguationData":[TD([[subQ2,-1.0]])],"derivedFrom":subQ1}),1.0]])]});}
            var Q1;
            {var subQ0=sQuery(id+"F0.wireOp",EDGE,"E17");var subQ5=sQuery(id+"F0.wireOp",EDGE,"E4");var subQ9=makeQuery(id+"F0.imprint","INTERSECT",VERTEX,{"disambiguationData":[OD(0.0)],"derivedFrom":[subQ5,subQ0]});Q1=makeQuery(id+"F0.imprint","IMPRINT",FACE,{"disambiguationData":[TD([[makeQuery(id+"F0.imprint","IMPRINT",EDGE,{"disambiguationData":[TD([[subQ9,-1.0]])],"derivedFrom":subQ5}),1.0]])]});}
            var Q2;
            {var subQ0=sQuery(id+"F0.wireOp",EDGE,"E17");var subQ1=sQuery(id+"F0.wireOp",EDGE,"E4");var subQ2=makeQuery(id+"F0.imprint","INTERSECT",VERTEX,{"disambiguationData":[OD(0.0)],"derivedFrom":[subQ1,subQ0]});Q2=makeQuery(id+"F0.imprint","IMPRINT",FACE,{"disambiguationData":[TD([[makeQuery(id+"F0.imprint","IMPRINT",EDGE,{"disambiguationData":[TD([[subQ2,-1.0]])],"derivedFrom":subQ1}),-1.0]])]});}
            var Q3;
            {var subQ0=sQuery(id+"F0.wireOp",EDGE,"E16");var subQ1=sQuery(id+"F0.wireOp",EDGE,"E14");var subQ2=makeQuery(id+"F0.imprint","INTERSECT",VERTEX,{"disambiguationData":[OD(0.0)],"derivedFrom":[subQ1,subQ0]});Q3=makeQuery(id+"F0.imprint","IMPRINT",FACE,{"disambiguationData":[TD([[makeQuery(id+"F0.imprint","IMPRINT",EDGE,{"disambiguationData":[TD([[subQ2,-1.0]])],"derivedFrom":subQ1}),1.0]])]});}
            var Q4;
            {var subQ1=sQuery(id+"F0.wireOp",EDGE,"E4");var subQ4=sQuery(id+"F0.wireOp",EDGE,"E16");var subQ9=makeQuery(id+"F0.imprint","INTERSECT",VERTEX,{"disambiguationData":[OD(0.0)],"derivedFrom":[subQ1,subQ4]});Q4=makeQuery(id+"F0.imprint","IMPRINT",FACE,{"disambiguationData":[TD([[makeQuery(id+"F0.imprint","IMPRINT",EDGE,{"disambiguationData":[TD([[subQ9,-1.0]])],"derivedFrom":subQ1}),1.0]])]});}
            var Q5;
            {var subQ0=sQuery(id+"F0.wireOp",EDGE,"E16");var subQ1=sQuery(id+"F0.wireOp",EDGE,"E4");var subQ2=makeQuery(id+"F0.imprint","INTERSECT",VERTEX,{"disambiguationData":[OD(0.0)],"derivedFrom":[subQ1,subQ0]});Q5=makeQuery(id+"F0.imprint","IMPRINT",FACE,{"disambiguationData":[TD([[makeQuery(id+"F0.imprint","IMPRINT",EDGE,{"disambiguationData":[TD([[subQ2,-1.0]])],"derivedFrom":subQ1}),-1.0]])]});}
            var Q6;
            {var subQ0=sQuery(id+"F0.wireOp",EDGE,"E15");var subQ1=sQuery(id+"F0.wireOp",EDGE,"E14");var subQ2=makeQuery(id+"F0.imprint","INTERSECT",VERTEX,{"disambiguationData":[OD(0.0)],"derivedFrom":[subQ1,subQ0]});Q6=makeQuery(id+"F0.imprint","IMPRINT",FACE,{"disambiguationData":[TD([[makeQuery(id+"F0.imprint","IMPRINT",EDGE,{"disambiguationData":[TD([[subQ2,-1.0]])],"derivedFrom":subQ1}),1.0]])]});}
            var Q7;
            {var subQ0=sQuery(id+"F0.wireOp",EDGE,"E15");var subQ5=sQuery(id+"F0.wireOp",EDGE,"E4");var subQ9=makeQuery(id+"F0.imprint","INTERSECT",VERTEX,{"disambiguationData":[OD(0.0)],"derivedFrom":[subQ5,subQ0]});Q7=makeQuery(id+"F0.imprint","IMPRINT",FACE,{"disambiguationData":[TD([[makeQuery(id+"F0.imprint","IMPRINT",EDGE,{"disambiguationData":[TD([[subQ9,-1.0]])],"derivedFrom":subQ5}),1.0]])]});}
            var Q8;
            {var subQ0=sQuery(id+"F0.wireOp",EDGE,"E15");var subQ1=sQuery(id+"F0.wireOp",EDGE,"E4");var subQ2=makeQuery(id+"F0.imprint","INTERSECT",VERTEX,{"disambiguationData":[OD(0.0)],"derivedFrom":[subQ1,subQ0]});Q8=makeQuery(id+"F0.imprint","IMPRINT",FACE,{"disambiguationData":[TD([[makeQuery(id+"F0.imprint","IMPRINT",EDGE,{"disambiguationData":[TD([[subQ2,-1.0]])],"derivedFrom":subQ1}),-1.0]])]});}
            extrude(context, id + "F6", {"entities" : qUnion([Q0, Q1, Q2, Q3, Q4, Q5, Q6, Q7, Q8]), "operationType" : NewBodyOperationType.ADD, "depth" : -1 * mm, "offsetDistance" : 25 * mm});
        }
        {
            var Q0;
            {var subQ0=sQuery(id+"F0.wireOp",EDGE,"E13");var subQ1=sQuery(id+"F0.wireOp",EDGE,"E4");var subQ2=makeQuery(id+"F0.imprint","INTERSECT",VERTEX,{"disambiguationData":[OD(0.0)],"derivedFrom":[subQ1,subQ0]});Q0=makeQuery(id+"F0.imprint","IMPRINT",FACE,{"disambiguationData":[TD([[makeQuery(id+"F0.imprint","IMPRINT",EDGE,{"disambiguationData":[TD([[subQ2,-1.0]])],"derivedFrom":subQ1}),-1.0]])]});}
            var Q1;
            {var subQ0=sQuery(id+"F0.wireOp",EDGE,"E13");var subQ1=sQuery(id+"F0.wireOp",EDGE,"E4");var subQ2=makeQuery(id+"F0.imprint","INTERSECT",VERTEX,{"disambiguationData":[OD(0.0)],"derivedFrom":[subQ1,subQ0]});Q1=makeQuery(id+"F0.imprint","IMPRINT",FACE,{"disambiguationData":[TD([[makeQuery(id+"F0.imprint","IMPRINT",EDGE,{"disambiguationData":[TD([[subQ2,-1.0]])],"derivedFrom":subQ1}),1.0]])]});}
            var Q2;
            {var subQ0=sQuery(id+"F0.wireOp",EDGE,"E11");var subQ1=sQuery(id+"F0.wireOp",EDGE,"E4");var subQ2=makeQuery(id+"F0.imprint","INTERSECT",VERTEX,{"disambiguationData":[OD(0.0)],"derivedFrom":[subQ1,subQ0]});Q2=makeQuery(id+"F0.imprint","IMPRINT",FACE,{"disambiguationData":[TD([[makeQuery(id+"F0.imprint","IMPRINT",EDGE,{"disambiguationData":[TD([[subQ2,-1.0]])],"derivedFrom":subQ1}),1.0]])]});}
            var Q3;
            {var subQ0=sQuery(id+"F0.wireOp",EDGE,"E11");var subQ1=sQuery(id+"F0.wireOp",EDGE,"E4");var subQ2=makeQuery(id+"F0.imprint","INTERSECT",VERTEX,{"disambiguationData":[OD(0.0)],"derivedFrom":[subQ1,subQ0]});Q3=makeQuery(id+"F0.imprint","IMPRINT",FACE,{"disambiguationData":[TD([[makeQuery(id+"F0.imprint","IMPRINT",EDGE,{"disambiguationData":[TD([[subQ2,-1.0]])],"derivedFrom":subQ1}),-1.0]])]});}
            var Q4;
            {var subQ0=sQuery(id+"F0.wireOp",EDGE,"E12");var subQ1=sQuery(id+"F0.wireOp",EDGE,"E4");var subQ2=makeQuery(id+"F0.imprint","INTERSECT",VERTEX,{"disambiguationData":[OD(0.0)],"derivedFrom":[subQ1,subQ0]});Q4=makeQuery(id+"F0.imprint","IMPRINT",FACE,{"disambiguationData":[TD([[makeQuery(id+"F0.imprint","IMPRINT",EDGE,{"disambiguationData":[TD([[subQ2,-1.0]])],"derivedFrom":subQ1}),1.0]])]});}
            var Q5;
            {var subQ0=sQuery(id+"F0.wireOp",EDGE,"E12");var subQ1=sQuery(id+"F0.wireOp",EDGE,"E4");var subQ2=makeQuery(id+"F0.imprint","INTERSECT",VERTEX,{"disambiguationData":[OD(0.0)],"derivedFrom":[subQ1,subQ0]});Q5=makeQuery(id+"F0.imprint","IMPRINT",FACE,{"disambiguationData":[TD([[makeQuery(id+"F0.imprint","IMPRINT",EDGE,{"disambiguationData":[TD([[subQ2,-1.0]])],"derivedFrom":subQ1}),-1.0]])]});}
            extrude(context, id + "F7", {"entities" : qUnion([Q0, Q1, Q2, Q3, Q4, Q5]), "operationType" : NewBodyOperationType.REMOVE, "depth" : 2 * mm, "offsetDistance" : 25 * mm});
        }
        {
            var Q0;
            {var subQ0=sQuery(id+"F0.wireOp",EDGE,"E22.left");var subQ1=sQuery(id+"F0.wireOp",EDGE,"E21");var subQ2=makeQuery(id+"F0.imprint","INTERSECT",VERTEX,{"disambiguationData":[OD(1.0)],"derivedFrom":[subQ1,subQ0]});Q0=makeQuery(id+"F0.imprint","IMPRINT",FACE,{"disambiguationData":[TD([[makeQuery(id+"F0.imprint","IMPRINT",EDGE,{"disambiguationData":[TD([[subQ2,-1.0]])],"derivedFrom":subQ1}),-1.0]])]});}
            var Q1;
            {var subQ0=sQuery(id+"F0.wireOp",EDGE,"E22.right");var subQ1=sQuery(id+"F0.wireOp",EDGE,"E21");var subQ2=makeQuery(id+"F0.imprint","INTERSECT",VERTEX,{"disambiguationData":[OD(1.0)],"derivedFrom":[subQ1,subQ0]});Q1=makeQuery(id+"F0.imprint","IMPRINT",FACE,{"disambiguationData":[TD([[makeQuery(id+"F0.imprint","IMPRINT",EDGE,{"disambiguationData":[TD([[subQ2,-1.0]])],"derivedFrom":subQ1}),-1.0]])]});}
            var Q2;
            {var subQ0=sQuery(id+"F0.wireOp",EDGE,"E23.bottom");var subQ1=sQuery(id+"F0.wireOp",EDGE,"E21");var subQ2=makeQuery(id+"F0.imprint","INTERSECT",VERTEX,{"disambiguationData":[OD(0.0)],"derivedFrom":[subQ1,subQ0]});Q2=makeQuery(id+"F0.imprint","IMPRINT",FACE,{"disambiguationData":[TD([[makeQuery(id+"F0.imprint","IMPRINT",EDGE,{"disambiguationData":[TD([[subQ2,-1.0]])],"derivedFrom":subQ1}),-1.0]])]});}
            var Q3;
            {var subQ0=sQuery(id+"F0.wireOp",EDGE,"E24.0");var subQ1=sQuery(id+"F0.wireOp",EDGE,"E3");var subQ2=makeQuery(id+"F0.imprint","INTERSECT",VERTEX,{"disambiguationData":[OD(0.0)],"derivedFrom":[subQ1,subQ0]});Q3=makeQuery(id+"F0.imprint","IMPRINT",FACE,{"disambiguationData":[TD([[makeQuery(id+"F0.imprint","IMPRINT",EDGE,{"disambiguationData":[TD([[subQ2,-1.0]])],"derivedFrom":subQ1}),-1.0]])]});}
            var Q4;
            {var subQ0=sQuery(id+"F0.wireOp",EDGE,"E23.right");var subQ1=sQuery(id+"F0.wireOp",EDGE,"E3");var subQ2=makeQuery(id+"F0.imprint","INTERSECT",VERTEX,{"derivedFrom":[subQ1,subQ0]});Q4=makeQuery(id+"F0.imprint","IMPRINT",FACE,{"disambiguationData":[TD([[makeQuery(id+"F0.imprint","IMPRINT",EDGE,{"disambiguationData":[TD([[subQ2,-1.0]])],"derivedFrom":subQ1}),-1.0]])]});}
            var Q5;
            {var subQ0=sQuery(id+"F0.wireOp",EDGE,"E23.right");var subQ1=sQuery(id+"F0.wireOp",EDGE,"E3");var subQ2=makeQuery(id+"F0.imprint","INTERSECT",VERTEX,{"derivedFrom":[subQ1,subQ0]});Q5=makeQuery(id+"F0.imprint","IMPRINT",FACE,{"disambiguationData":[TD([[makeQuery(id+"F0.imprint","IMPRINT",EDGE,{"disambiguationData":[TD([[subQ2,-1.0]])],"derivedFrom":subQ1}),1.0]])]});}
            var Q6;
            {var subQ0=sQuery(id+"F0.wireOp",EDGE,"E24.0");var subQ1=sQuery(id+"F0.wireOp",EDGE,"E3");var subQ2=makeQuery(id+"F0.imprint","INTERSECT",VERTEX,{"disambiguationData":[OD(0.0)],"derivedFrom":[subQ1,subQ0]});Q6=makeQuery(id+"F0.imprint","IMPRINT",FACE,{"disambiguationData":[TD([[makeQuery(id+"F0.imprint","IMPRINT",EDGE,{"disambiguationData":[TD([[subQ2,-1.0]])],"derivedFrom":subQ1}),1.0]])]});}
            var Q7;
            {var subQ0=sQuery(id+"F0.wireOp",EDGE,"E22.right");var subQ1=sQuery(id+"F0.wireOp",EDGE,"E21");var subQ2=makeQuery(id+"F0.imprint","INTERSECT",VERTEX,{"disambiguationData":[OD(0.0)],"derivedFrom":[subQ1,subQ0]});Q7=makeQuery(id+"F0.imprint","IMPRINT",FACE,{"disambiguationData":[TD([[makeQuery(id+"F0.imprint","IMPRINT",EDGE,{"disambiguationData":[TD([[subQ2,-1.0]])],"derivedFrom":subQ1}),-1.0]])]});}
            var Q8;
            {var subQ0=sQuery(id+"F0.wireOp",EDGE,"E22.left");var subQ1=sQuery(id+"F0.wireOp",EDGE,"E21");var subQ2=makeQuery(id+"F0.imprint","INTERSECT",VERTEX,{"disambiguationData":[OD(0.0)],"derivedFrom":[subQ1,subQ0]});Q8=makeQuery(id+"F0.imprint","IMPRINT",FACE,{"disambiguationData":[TD([[makeQuery(id+"F0.imprint","IMPRINT",EDGE,{"disambiguationData":[TD([[subQ2,-1.0]])],"derivedFrom":subQ1}),-1.0]])]});}
            var Q9;
            {var subQ0=sQuery(id+"F0.wireOp",EDGE,"E22.top");Q9=makeQuery(id+"F0.imprint","IMPRINT",FACE,{"disambiguationData":[TD([[makeQuery(id+"F0.imprint","IMPRINT",EDGE,{"derivedFrom":subQ0}),1.0]])]});}
            var Q10;
            {var subQ0=sQuery(id+"F0.wireOp",EDGE,"E23.top");var subQ1=sQuery(id+"F0.wireOp",EDGE,"E21");var subQ2=makeQuery(id+"F0.imprint","INTERSECT",VERTEX,{"disambiguationData":[OD(0.0)],"derivedFrom":[subQ1,subQ0]});Q10=makeQuery(id+"F0.imprint","IMPRINT",FACE,{"disambiguationData":[TD([[makeQuery(id+"F0.imprint","IMPRINT",EDGE,{"disambiguationData":[TD([[subQ2,-1.0]])],"derivedFrom":subQ1}),-1.0]])]});}
            var Q11;
            {var subQ0=sQuery(id+"F0.wireOp",EDGE,"E24.0");var subQ1=sQuery(id+"F0.wireOp",EDGE,"E3");var subQ2=makeQuery(id+"F0.imprint","INTERSECT",VERTEX,{"disambiguationData":[OD(1.0)],"derivedFrom":[subQ1,subQ0]});Q11=makeQuery(id+"F0.imprint","IMPRINT",FACE,{"disambiguationData":[TD([[makeQuery(id+"F0.imprint","IMPRINT",EDGE,{"disambiguationData":[TD([[subQ2,-1.0]])],"derivedFrom":subQ1}),-1.0]])]});}
            var Q12;
            {var subQ0=sQuery(id+"F0.wireOp",EDGE,"E21");var subQ1=sQuery(id+"F0.wireOp",EDGE,"E3");var subQ2=makeQuery(id+"F0.imprint","INTERSECT",VERTEX,{"disambiguationData":[OD(1.0)],"derivedFrom":[subQ1,subQ0]});Q12=makeQuery(id+"F0.imprint","IMPRINT",FACE,{"disambiguationData":[TD([[makeQuery(id+"F0.imprint","IMPRINT",EDGE,{"disambiguationData":[TD([[subQ2,-1.0]])],"derivedFrom":subQ1}),-1.0]])]});}
            var Q13;
            {var subQ0=sQuery(id+"F0.wireOp",EDGE,"E21");var subQ1=sQuery(id+"F0.wireOp",EDGE,"E3");var subQ2=makeQuery(id+"F0.imprint","INTERSECT",VERTEX,{"disambiguationData":[OD(1.0)],"derivedFrom":[subQ1,subQ0]});Q13=makeQuery(id+"F0.imprint","IMPRINT",FACE,{"disambiguationData":[TD([[makeQuery(id+"F0.imprint","IMPRINT",EDGE,{"disambiguationData":[TD([[subQ2,-1.0]])],"derivedFrom":subQ1}),1.0]])]});}
            var Q14;
            {var subQ0=sQuery(id+"F0.wireOp",EDGE,"E24.0");var subQ1=sQuery(id+"F0.wireOp",EDGE,"E3");var subQ2=makeQuery(id+"F0.imprint","INTERSECT",VERTEX,{"disambiguationData":[OD(1.0)],"derivedFrom":[subQ1,subQ0]});Q14=makeQuery(id+"F0.imprint","IMPRINT",FACE,{"disambiguationData":[TD([[makeQuery(id+"F0.imprint","IMPRINT",EDGE,{"disambiguationData":[TD([[subQ2,-1.0]])],"derivedFrom":subQ1}),1.0]])]});}
            var Q15;
            {var subQ0=sQuery(id+"F0.wireOp",EDGE,"E22.bottom");Q15=makeQuery(id+"F0.imprint","IMPRINT",FACE,{"disambiguationData":[TD([[makeQuery(id+"F0.imprint","IMPRINT",EDGE,{"derivedFrom":subQ0}),-1.0]])]});}
            extrude(context, id + "F8", {"entities" : qUnion([Q0, Q1, Q2, Q3, Q4, Q5, Q6, Q7, Q8, Q9, Q10, Q11, Q12, Q13, Q14, Q15]), "operationType" : NewBodyOperationType.ADD, "depth" : 15 * mm, "offsetDistance" : 25 * mm});
        }
        {
            var Q0;
            Q0=makeQuery(id+"F0.imprint","IMPRINT",FACE,{"disambiguationData":[TD([[makeQuery(id+"F0.imprint","IMPRINT",EDGE,{"derivedFrom":sQuery(id+"F0.wireOp",EDGE,"E22.bottom")}),1.0]])]});
            var Q1;
            {var subQ0=sQuery(id+"F0.wireOp",EDGE,"E22.bottom");Q1=makeQuery(id+"F0.imprint","IMPRINT",FACE,{"disambiguationData":[TD([[makeQuery(id+"F0.imprint","IMPRINT",EDGE,{"derivedFrom":subQ0}),-1.0]])]});}
            var Q2;
            {var subQ0=sQuery(id+"F0.wireOp",EDGE,"E22.left");var subQ1=sQuery(id+"F0.wireOp",EDGE,"E21");var subQ2=makeQuery(id+"F0.imprint","INTERSECT",VERTEX,{"disambiguationData":[OD(0.0)],"derivedFrom":[subQ1,subQ0]});Q2=makeQuery(id+"F0.imprint","IMPRINT",FACE,{"disambiguationData":[TD([[makeQuery(id+"F0.imprint","IMPRINT",EDGE,{"disambiguationData":[TD([[subQ2,-1.0]])],"derivedFrom":subQ1}),-1.0]])]});}
            var Q3;
            {var subQ0=sQuery(id+"F0.wireOp",EDGE,"E22.top");Q3=makeQuery(id+"F0.imprint","IMPRINT",FACE,{"disambiguationData":[TD([[makeQuery(id+"F0.imprint","IMPRINT",EDGE,{"derivedFrom":subQ0}),1.0]])]});}
            var Q4;
            {var subQ0=sQuery(id+"F0.wireOp",EDGE,"E22.right");var subQ1=sQuery(id+"F0.wireOp",EDGE,"E21");var subQ2=makeQuery(id+"F0.imprint","INTERSECT",VERTEX,{"disambiguationData":[OD(1.0)],"derivedFrom":[subQ1,subQ0]});Q4=makeQuery(id+"F0.imprint","IMPRINT",FACE,{"disambiguationData":[TD([[makeQuery(id+"F0.imprint","IMPRINT",EDGE,{"disambiguationData":[TD([[subQ2,-1.0]])],"derivedFrom":subQ1}),-1.0]])]});}
            var Q5;
            {var subQ0=sQuery(id+"F0.wireOp",EDGE,"E22.left");var subQ1=sQuery(id+"F0.wireOp",EDGE,"E21");var subQ2=makeQuery(id+"F0.imprint","INTERSECT",VERTEX,{"disambiguationData":[OD(1.0)],"derivedFrom":[subQ1,subQ0]});Q5=makeQuery(id+"F0.imprint","IMPRINT",FACE,{"disambiguationData":[TD([[makeQuery(id+"F0.imprint","IMPRINT",EDGE,{"disambiguationData":[TD([[subQ2,-1.0]])],"derivedFrom":subQ1}),-1.0]])]});}
            var Q6;
            {var subQ0=sQuery(id+"F0.wireOp",EDGE,"E21");var subQ1=sQuery(id+"F0.wireOp",EDGE,"E3");var subQ2=makeQuery(id+"F0.imprint","INTERSECT",VERTEX,{"disambiguationData":[OD(1.0)],"derivedFrom":[subQ1,subQ0]});Q6=makeQuery(id+"F0.imprint","IMPRINT",FACE,{"disambiguationData":[TD([[makeQuery(id+"F0.imprint","IMPRINT",EDGE,{"disambiguationData":[TD([[subQ2,-1.0]])],"derivedFrom":subQ1}),-1.0]])]});}
            var Q7;
            {var subQ0=sQuery(id+"F0.wireOp",EDGE,"E21");var subQ1=sQuery(id+"F0.wireOp",EDGE,"E3");var subQ2=makeQuery(id+"F0.imprint","INTERSECT",VERTEX,{"disambiguationData":[OD(1.0)],"derivedFrom":[subQ1,subQ0]});Q7=makeQuery(id+"F0.imprint","IMPRINT",FACE,{"disambiguationData":[TD([[makeQuery(id+"F0.imprint","IMPRINT",EDGE,{"disambiguationData":[TD([[subQ2,-1.0]])],"derivedFrom":subQ1}),1.0]])]});}
            var Q8;
            {var subQ0=sQuery(id+"F0.wireOp",EDGE,"E23.top");var subQ1=sQuery(id+"F0.wireOp",EDGE,"E21");var subQ2=makeQuery(id+"F0.imprint","INTERSECT",VERTEX,{"disambiguationData":[OD(0.0)],"derivedFrom":[subQ1,subQ0]});Q8=makeQuery(id+"F0.imprint","IMPRINT",FACE,{"disambiguationData":[TD([[makeQuery(id+"F0.imprint","IMPRINT",EDGE,{"disambiguationData":[TD([[subQ2,-1.0]])],"derivedFrom":subQ1}),-1.0]])]});}
            var Q9;
            {var subQ0=sQuery(id+"F0.wireOp",EDGE,"E22.right");var subQ1=sQuery(id+"F0.wireOp",EDGE,"E21");var subQ2=makeQuery(id+"F0.imprint","INTERSECT",VERTEX,{"disambiguationData":[OD(0.0)],"derivedFrom":[subQ1,subQ0]});Q9=makeQuery(id+"F0.imprint","IMPRINT",FACE,{"disambiguationData":[TD([[makeQuery(id+"F0.imprint","IMPRINT",EDGE,{"disambiguationData":[TD([[subQ2,-1.0]])],"derivedFrom":subQ1}),-1.0]])]});}
            var Q10;
            {var subQ0=sQuery(id+"F0.wireOp",EDGE,"E24.0");var subQ1=sQuery(id+"F0.wireOp",EDGE,"E3");var subQ2=makeQuery(id+"F0.imprint","INTERSECT",VERTEX,{"disambiguationData":[OD(0.0)],"derivedFrom":[subQ1,subQ0]});Q10=makeQuery(id+"F0.imprint","IMPRINT",FACE,{"disambiguationData":[TD([[makeQuery(id+"F0.imprint","IMPRINT",EDGE,{"disambiguationData":[TD([[subQ2,-1.0]])],"derivedFrom":subQ1}),1.0]])]});}
            var Q11;
            {var subQ0=sQuery(id+"F0.wireOp",EDGE,"E24.0");var subQ1=sQuery(id+"F0.wireOp",EDGE,"E3");var subQ2=makeQuery(id+"F0.imprint","INTERSECT",VERTEX,{"disambiguationData":[OD(0.0)],"derivedFrom":[subQ1,subQ0]});Q11=makeQuery(id+"F0.imprint","IMPRINT",FACE,{"disambiguationData":[TD([[makeQuery(id+"F0.imprint","IMPRINT",EDGE,{"disambiguationData":[TD([[subQ2,-1.0]])],"derivedFrom":subQ1}),-1.0]])]});}
            var Q12;
            {var subQ0=sQuery(id+"F0.wireOp",EDGE,"E23.bottom");var subQ1=sQuery(id+"F0.wireOp",EDGE,"E21");var subQ2=makeQuery(id+"F0.imprint","INTERSECT",VERTEX,{"disambiguationData":[OD(0.0)],"derivedFrom":[subQ1,subQ0]});Q12=makeQuery(id+"F0.imprint","IMPRINT",FACE,{"disambiguationData":[TD([[makeQuery(id+"F0.imprint","IMPRINT",EDGE,{"disambiguationData":[TD([[subQ2,-1.0]])],"derivedFrom":subQ1}),-1.0]])]});}
            var Q13;
            {var subQ0=sQuery(id+"F0.wireOp",EDGE,"E25");Q13=makeQuery(id+"F0.imprint","IMPRINT",FACE,{"disambiguationData":[TD([[makeQuery(id+"F0.imprint","IMPRINT",EDGE,{"derivedFrom":subQ0}),-1.0]])]});}
            var Q14;
            {var subQ0=sQuery(id+"F0.wireOp",EDGE,"E26");Q14=makeQuery(id+"F0.imprint","IMPRINT",FACE,{"disambiguationData":[TD([[makeQuery(id+"F0.imprint","IMPRINT",EDGE,{"derivedFrom":subQ0}),1.0]])]});}
            var Q15;
            {var subQ0=sQuery(id+"F0.wireOp",EDGE,"E23.right");var subQ1=sQuery(id+"F0.wireOp",EDGE,"E3");var subQ2=makeQuery(id+"F0.imprint","INTERSECT",VERTEX,{"derivedFrom":[subQ1,subQ0]});Q15=makeQuery(id+"F0.imprint","IMPRINT",FACE,{"disambiguationData":[TD([[makeQuery(id+"F0.imprint","IMPRINT",EDGE,{"disambiguationData":[TD([[subQ2,-1.0]])],"derivedFrom":subQ1}),1.0]])]});}
            var Q16;
            {var subQ0=sQuery(id+"F0.wireOp",EDGE,"E23.right");var subQ1=sQuery(id+"F0.wireOp",EDGE,"E3");var subQ2=makeQuery(id+"F0.imprint","INTERSECT",VERTEX,{"derivedFrom":[subQ1,subQ0]});Q16=makeQuery(id+"F0.imprint","IMPRINT",FACE,{"disambiguationData":[TD([[makeQuery(id+"F0.imprint","IMPRINT",EDGE,{"disambiguationData":[TD([[subQ2,-1.0]])],"derivedFrom":subQ1}),-1.0]])]});}
            var Q17;
            {var subQ0=sQuery(id+"F0.wireOp",EDGE,"E24.0");var subQ1=sQuery(id+"F0.wireOp",EDGE,"E3");var subQ2=makeQuery(id+"F0.imprint","INTERSECT",VERTEX,{"disambiguationData":[OD(1.0)],"derivedFrom":[subQ1,subQ0]});Q17=makeQuery(id+"F0.imprint","IMPRINT",FACE,{"disambiguationData":[TD([[makeQuery(id+"F0.imprint","IMPRINT",EDGE,{"disambiguationData":[TD([[subQ2,-1.0]])],"derivedFrom":subQ1}),-1.0]])]});}
            var Q18;
            {var subQ0=sQuery(id+"F0.wireOp",EDGE,"E24.0");var subQ1=sQuery(id+"F0.wireOp",EDGE,"E3");var subQ2=makeQuery(id+"F0.imprint","INTERSECT",VERTEX,{"disambiguationData":[OD(1.0)],"derivedFrom":[subQ1,subQ0]});Q18=makeQuery(id+"F0.imprint","IMPRINT",FACE,{"disambiguationData":[TD([[makeQuery(id+"F0.imprint","IMPRINT",EDGE,{"disambiguationData":[TD([[subQ2,-1.0]])],"derivedFrom":subQ1}),1.0]])]});}
            var Q19;
            {var subQ0=sQuery(id+"F0.wireOp",EDGE,"E28");Q19=makeQuery(id+"F0.imprint","IMPRINT",FACE,{"disambiguationData":[TD([[makeQuery(id+"F0.imprint","IMPRINT",EDGE,{"derivedFrom":subQ0}),-1.0]])]});}
            var Q20;
            {var subQ0=sQuery(id+"F0.wireOp",EDGE,"E27");Q20=makeQuery(id+"F0.imprint","IMPRINT",FACE,{"disambiguationData":[TD([[makeQuery(id+"F0.imprint","IMPRINT",EDGE,{"derivedFrom":subQ0}),1.0]])]});}
            var Q21;
            Q21=makeQuery(id+"F0.imprint","IMPRINT",FACE,{"disambiguationData":[TD([[makeQuery(id+"F0.imprint","IMPRINT",EDGE,{"derivedFrom":sQuery(id+"F0.wireOp",EDGE,"E22.top")}),-1.0]])]});
            extrude(context, id + "F9", {"entities" : qUnion([Q0, Q1, Q2, Q3, Q4, Q5, Q6, Q7, Q8, Q9, Q10, Q11, Q12, Q13, Q14, Q15, Q16, Q17, Q18, Q19, Q20, Q21]), "depth" : 4 * mm, "offsetDistance" : 25 * mm});
        }
        {
            var Q0;
            Q0=makeQuery(id+"F2.opExtrude","CAP_FACE",FACE,{"disambiguationData":[OSD([sQuery(id+"F0.wireOp",EDGE,"E1"),sQuery(id+"F0.wireOp",EDGE,"E2.0")])],"isStart":false});
            cPlane(context, id + "F10", {"entities" : qUnion([Q0]), "cplaneType" : CPlaneType.OFFSET, "offset" : 0 * mm, "width" : 150 * mm, "height" : 150 * mm});
        }
        {
            var Q0;
            Q0=qCreatedBy(id+"F10.planeOp",FACE);
            var sketch = newSketch(context, id + "F11", { "sketchPlane" : qUnion([Q0])});
            skCircle(sketch, "E33", {"center": v(0, 0) * mm, "radius": 7.5 * mm});
            skCircle(sketch, "E34", {"center": v(0, 0) * mm, "radius": 6.5 * mm});
            skLineSegment(sketch, "E35", {"start": v(-4.98, -4.18) * mm, "end": v(-5.74, -4.83) * mm});
            skLineSegment(sketch, "E36", {"start": v(-3.29, -5.6) * mm, "end": v(-3.92, -6.4) * mm});
            skLineSegment(sketch, "E37", {"start": v(3.29, -5.6) * mm, "end": v(3.92, -6.4) * mm});
            skLineSegment(sketch, "E38", {"start": v(4.98, -4.18) * mm, "end": v(5.67, -4.91) * mm});
            skLineSegment(sketch, "E39", {"start": v(4.98, 4.18) * mm, "end": v(5.66, 4.92) * mm});
            skLineSegment(sketch, "E40", {"start": v(3.29, 5.6) * mm, "end": v(3.87, 6.42) * mm});
            skLineSegment(sketch, "E41", {"start": v(-4.98, 4.18) * mm, "end": v(-5.63, 4.95) * mm});
            skLineSegment(sketch, "E42", {"start": v(-3.29, 5.6) * mm, "end": v(-3.94, 6.38) * mm});
            skSolve(sketch);
        }
        {
            var Q0;
            {var subQ0=sQuery(id+"F11.wireOp",EDGE,"E37");Q0=makeQuery(id+"F11.imprint","IMPRINT",FACE,{"disambiguationData":[TD([[makeQuery(id+"F11.imprint","IMPRINT",EDGE,{"derivedFrom":subQ0}),1.0]])]});}
            var Q1;
            {var subQ0=sQuery(id+"F11.wireOp",EDGE,"E35");Q1=makeQuery(id+"F11.imprint","IMPRINT",FACE,{"disambiguationData":[TD([[makeQuery(id+"F11.imprint","IMPRINT",EDGE,{"derivedFrom":subQ0}),1.0]])]});}
            var Q2;
            {var subQ0=sQuery(id+"F11.wireOp",EDGE,"E39");Q2=makeQuery(id+"F11.imprint","IMPRINT",FACE,{"disambiguationData":[TD([[makeQuery(id+"F11.imprint","IMPRINT",EDGE,{"derivedFrom":subQ0}),1.0]])]});}
            var Q3;
            {var subQ0=sQuery(id+"F11.wireOp",EDGE,"E41");Q3=makeQuery(id+"F11.imprint","IMPRINT",FACE,{"disambiguationData":[TD([[makeQuery(id+"F11.imprint","IMPRINT",EDGE,{"derivedFrom":subQ0}),-1.0]])]});}
            extrude(context, id + "F12", {"entities" : qUnion([Q0, Q1, Q2, Q3]), "operationType" : NewBodyOperationType.ADD, "oppositeDirection" : true, "depth" : 1 * mm, "offsetDistance" : 25 * mm});
        }
        {
            var Q0;
            {var subQ0=sQuery(id+"F0.wireOp",EDGE,"E1");Q0=makeQuery(id+"F2.boolean.opBoolean","MERGE",FACE,{"derivedFrom":[makeQuery(id+"F1.opExtrude","CAP_FACE",FACE,{"disambiguationData":[OSD([sQuery(id+"F0.wireOp",EDGE,"E0"),subQ0,sQuery(id+"F0.wireOp",EDGE,"E5"),sQuery(id+"F0.wireOp",EDGE,"E6"),sQuery(id+"F0.wireOp",EDGE,"E7"),sQuery(id+"F0.wireOp",EDGE,"E15"),sQuery(id+"F0.wireOp",EDGE,"E16"),sQuery(id+"F0.wireOp",EDGE,"E17")])],"isStart":true}),makeQuery(id+"F2.opExtrude","CAP_FACE",FACE,{"disambiguationData":[OSD([subQ0,sQuery(id+"F0.wireOp",EDGE,"E2.0")])],"isStart":true})]});}
            cPlane(context, id + "F13", {"entities" : qUnion([Q0]), "cplaneType" : CPlaneType.OFFSET, "offset" : 4 * mm, "oppositeDirection" : true, "width" : 150 * mm, "height" : 150 * mm});
        }
        {
            var Q0;
            Q0=qCreatedBy(id+"F13.planeOp",FACE);
            var sketch = newSketch(context, id + "F14", { "sketchPlane" : qUnion([Q0])});
            skCircle(sketch, "E43", {"center": v(0, 0) * mm, "radius": 7.5 * mm});
            skCircle(sketch, "E44", {"center": v(0, 0) * mm, "radius": 2.5 * mm});
            skSolve(sketch);
        }
        {
            var Q0;
            Q0 = qSketchRegion(id + "F14", true);
            extrude(context, id + "F15", {"entities" : qUnion([Q0]), "depth" : 2 * mm, "offsetDistance" : 25 * mm});
        }
        {
            var Q0;
            {var subQ0=sQuery(id+"F11.wireOp",EDGE,"E35");Q0=makeQuery(id+"F11.imprint","IMPRINT",FACE,{"disambiguationData":[TD([[makeQuery(id+"F11.imprint","IMPRINT",EDGE,{"derivedFrom":subQ0}),1.0]])]});}
            var Q1;
            {var subQ0=sQuery(id+"F11.wireOp",EDGE,"E37");Q1=makeQuery(id+"F11.imprint","IMPRINT",FACE,{"disambiguationData":[TD([[makeQuery(id+"F11.imprint","IMPRINT",EDGE,{"derivedFrom":subQ0}),1.0]])]});}
            var Q2;
            {var subQ0=sQuery(id+"F11.wireOp",EDGE,"E39");Q2=makeQuery(id+"F11.imprint","IMPRINT",FACE,{"disambiguationData":[TD([[makeQuery(id+"F11.imprint","IMPRINT",EDGE,{"derivedFrom":subQ0}),1.0]])]});}
            var Q3;
            {var subQ0=sQuery(id+"F11.wireOp",EDGE,"E41");Q3=makeQuery(id+"F11.imprint","IMPRINT",FACE,{"disambiguationData":[TD([[makeQuery(id+"F11.imprint","IMPRINT",EDGE,{"derivedFrom":subQ0}),-1.0]])]});}
            extrude(context, id + "F16", {"entities" : qUnion([Q0, Q1, Q2, Q3]), "operationType" : NewBodyOperationType.REMOVE, "endBound" : BoundingType.THROUGH_ALL, "oppositeDirection" : true, "depth" : 25 * mm, "offsetDistance" : 25 * mm});
        }
    });
